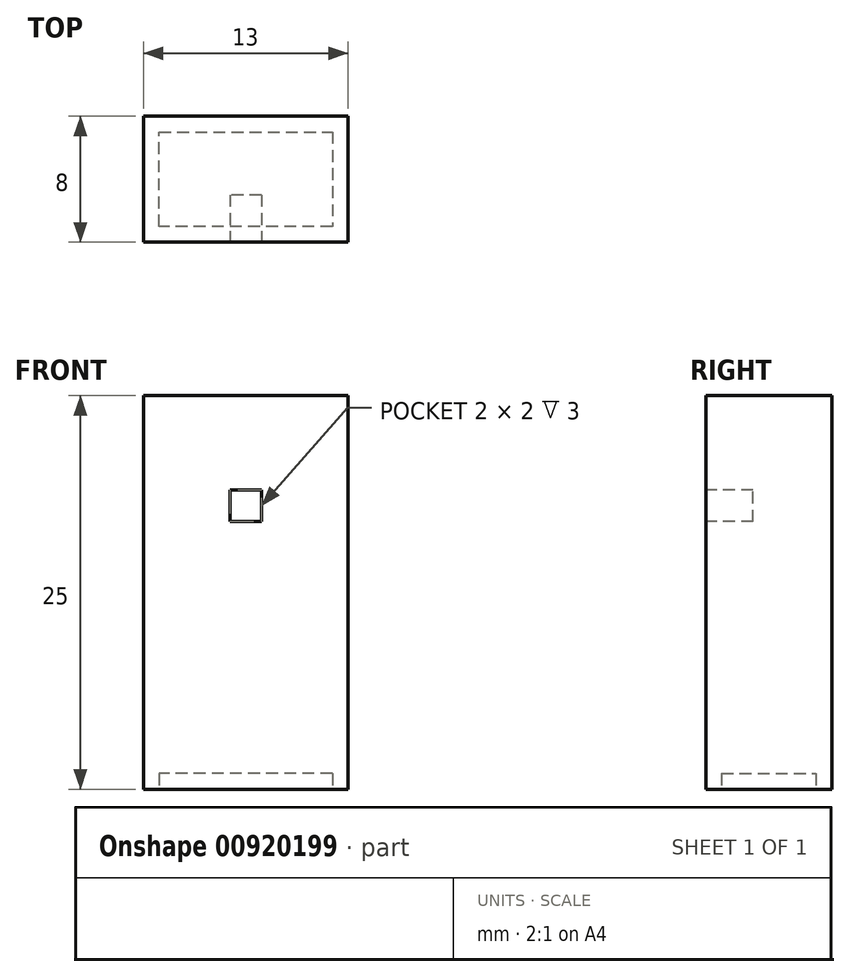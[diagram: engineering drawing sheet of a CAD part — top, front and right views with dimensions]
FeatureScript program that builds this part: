
annotation { "Feature Type Name" : "Feature", "Feature Type Description" : "" }
export const myFeature = defineFeature(function(context is Context, id is Id, definition is map)
    precondition{}
    {
        {
            var Q0;
            Q0=qCreatedBy(makeId("Top.planeOp"),FACE);
            var sketch = newSketch(context, id + "F0", { "sketchPlane" : qUnion([Q0])});
            skLineSegment(sketch, "E0.bottom", {"start": v(-6.5, 4) * mm, "end": v(6.5, 4) * mm});
            skLineSegment(sketch, "E0.top", {"start": v(-6.5, -4) * mm, "end": v(6.5, -4) * mm});
            skLineSegment(sketch, "E0.left", {"start": v(-6.5, 4) * mm, "end": v(-6.5, -4) * mm});
            skLineSegment(sketch, "E0.right", {"start": v(6.5, 4) * mm, "end": v(6.5, -4) * mm});
            skSolve(sketch);
        }
        {
            var Q0;
            Q0=makeQuery(id+"F0.imprint","IMPRINT",FACE,{"disambiguationData":[TD([[makeQuery(id+"F0.imprint","IMPRINT",EDGE,{"derivedFrom":sQuery(id+"F0.wireOp",EDGE,"E0.bottom")}),-1.0]])]});
            extrude(context, id + "F1", {"entities" : qUnion([Q0]), "depth" : 25 * mm, "offsetDistance" : 25 * mm});
        }
        {
            var Q0;
            Q0=makeQuery(id+"F1.opExtrude","CAP_FACE",FACE,{"disambiguationData":[OSD([sQuery(id+"F0.wireOp",EDGE,"E0.bottom"),sQuery(id+"F0.wireOp",EDGE,"E0.top"),sQuery(id+"F0.wireOp",EDGE,"E0.left"),sQuery(id+"F0.wireOp",EDGE,"E0.right")])],"isStart":true});
            var sketch = newSketch(context, id + "F2", { "sketchPlane" : qUnion([Q0])});
            skLineSegment(sketch, "E1.0.0", {"start": v(-6.5, 4) * mm, "end": v(-6.5, -4) * mm});
            skLineSegment(sketch, "E1.0.1", {"start": v(-6.5, -4) * mm, "end": v(6.5, -4) * mm});
            skLineSegment(sketch, "E1.0.2", {"start": v(6.5, -4) * mm, "end": v(6.5, 4) * mm});
            skLineSegment(sketch, "E1.0.3", {"start": v(6.5, 4) * mm, "end": v(-6.5, 4) * mm});
            skLineSegment(sketch, "E2.0", {"start": v(-5.5, 3) * mm, "end": v(-5.5, -3) * mm});
            skLineSegment(sketch, "E2.1", {"start": v(5.5, 3) * mm, "end": v(-5.5, 3) * mm});
            skLineSegment(sketch, "E2.2", {"start": v(5.5, -3) * mm, "end": v(5.5, 3) * mm});
            skLineSegment(sketch, "E2.3", {"start": v(-5.5, -3) * mm, "end": v(5.5, -3) * mm});
            skSolve(sketch);
        }
        {
            var Q0;
            Q0=makeQuery(id+"F2.imprint","IMPRINT",FACE,{"disambiguationData":[TD([[makeQuery(id+"F2.imprint","IMPRINT",EDGE,{"derivedFrom":sQuery(id+"F2.wireOp",EDGE,"E2.0")}),1.0]])]});
            extrude(context, id + "F3", {"entities" : qUnion([Q0]), "operationType" : NewBodyOperationType.REMOVE, "oppositeDirection" : true, "depth" : 1 * mm, "offsetDistance" : 25 * mm});
        }
        {
            var Q0;
            Q0=makeQuery(id+"F1.opExtrude","SWEPT_FACE",FACE,{"disambiguationData":[OSD([sQuery(id+"F0.wireOp",EDGE,"E0.top")])]});
            var sketch = newSketch(context, id + "F4", { "sketchPlane" : qUnion([Q0])});
            skLineSegment(sketch, "E3.bottom", {"start": v(1, 17) * mm, "end": v(-1, 17) * mm});
            skLineSegment(sketch, "E3.top", {"start": v(1, 19) * mm, "end": v(-1, 19) * mm});
            skLineSegment(sketch, "E3.left", {"start": v(1, 17) * mm, "end": v(1, 19) * mm});
            skLineSegment(sketch, "E3.right", {"start": v(-1, 17) * mm, "end": v(-1, 19) * mm});
            skPoint(sketch, "E3.middle", {"position": v(0, 18) * mm});
            skSolve(sketch);
        }
        {
            var Q0;
            Q0=makeQuery(id+"F4.imprint","IMPRINT",FACE,{"disambiguationData":[TD([[makeQuery(id+"F4.imprint","IMPRINT",EDGE,{"derivedFrom":sQuery(id+"F4.wireOp",EDGE,"E3.bottom")}),-1.0]])]});
            extrude(context, id + "F5", {"entities" : qUnion([Q0]), "operationType" : NewBodyOperationType.REMOVE, "oppositeDirection" : true, "depth" : 3 * mm, "offsetDistance" : 25 * mm});
        }
    });
